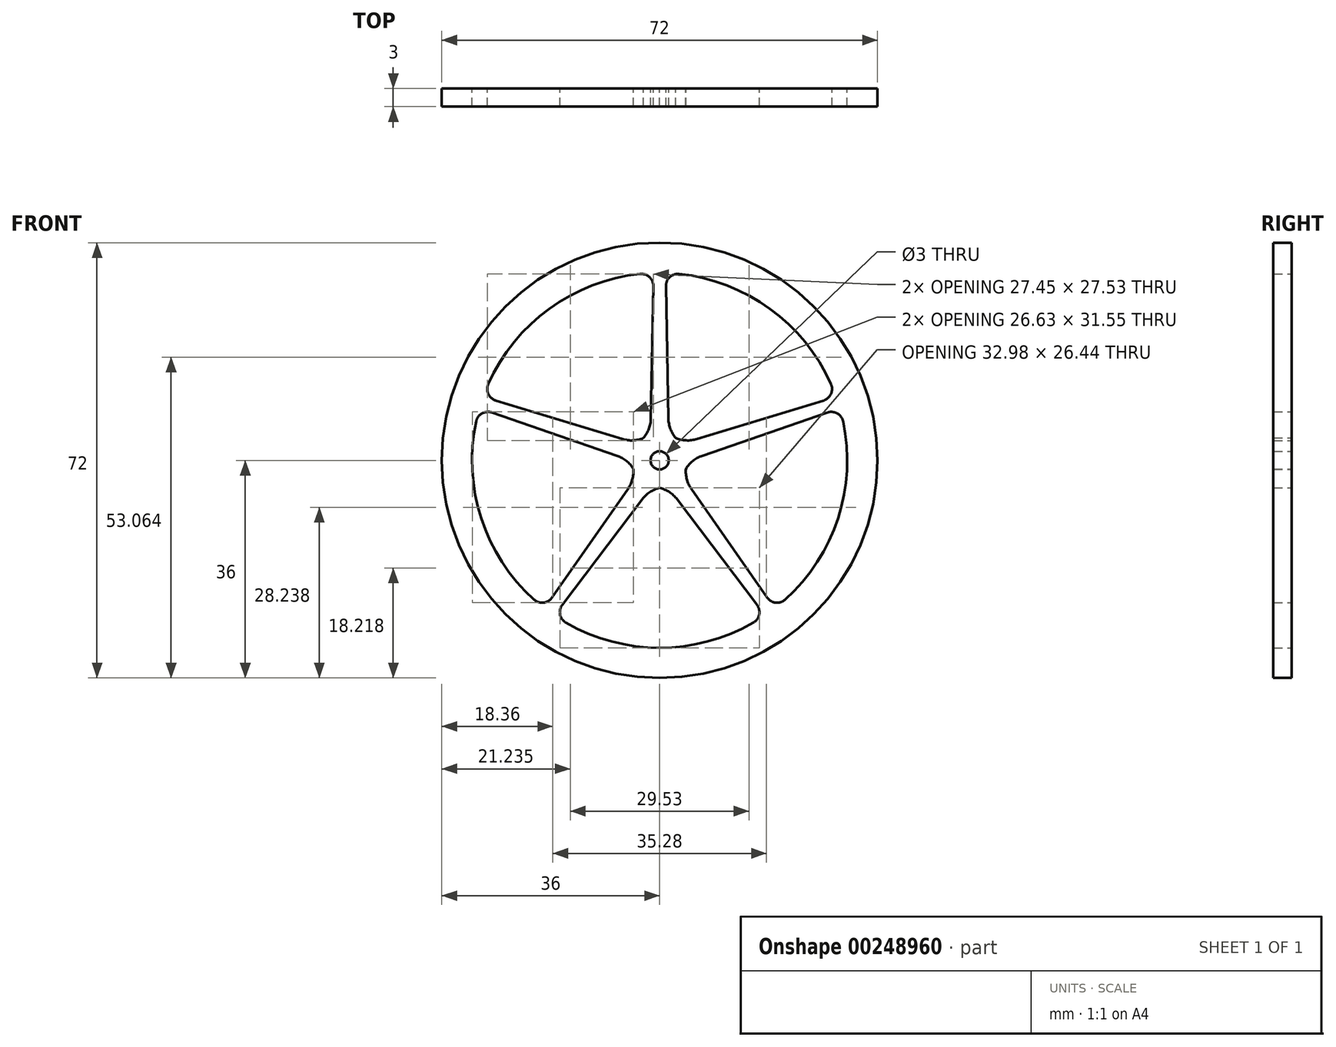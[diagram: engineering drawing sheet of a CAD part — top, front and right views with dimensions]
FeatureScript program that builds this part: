
annotation { "Feature Type Name" : "Feature", "Feature Type Description" : "" }
export const myFeature = defineFeature(function(context is Context, id is Id, definition is map)
    precondition{}
    {
        {
            var Q0;
            Q0=qCreatedBy(makeId("Front.planeOp"),FACE);
            var sketch = newSketch(context, id + "F0", { "sketchPlane" : qUnion([Q0])});
            skCircle(sketch, "E0", {"center": v(0, 0) * mm, "radius": 36 * mm});
            skCircle(sketch, "E1", {"center": v(0, 0) * mm, "radius": 1.5 * mm});
            skCircle(sketch, "E2", {"center": v(0, 0) * mm, "radius": 4.5 * mm});
            skCircle(sketch, "E3", {"center": v(0, 0) * mm, "radius": 31 * mm});
            skLineSegment(sketch, "E4", {"start": v(0, 0) * mm, "end": v(0, 1.5) * mm, "construction": true});
            skLineSegment(sketch, "E5", {"start": v(-1.5, 4.24) * mm, "end": v(-1, 30.98) * mm});
            skLineSegment(sketch, "E6.MirrorCS", {"start": v(1.5, 4.24) * mm, "end": v(1, 30.98) * mm});
            skPoint(sketch, "E7.trimOffspring.end.orphan", {"position": v(0, 31) * mm});
            skPoint(sketch, "E7.trimOffspring.start.orphan", {"position": v(0, 4.5) * mm});
            skSolve(sketch);
        }
        {
            var Q0;
            Q0=makeQuery(id+"F0.imprint","IMPRINT",FACE,{"disambiguationData":[TD([[makeQuery(id+"F0.imprint","IMPRINT",EDGE,{"derivedFrom":sQuery(id+"F0.wireOp",EDGE,"E0")}),1.0]])]});
            var Q1;
            {var subQ0=sQuery(id+"F0.wireOp",EDGE,"E5");Q1=makeQuery(id+"F0.imprint","IMPRINT",FACE,{"disambiguationData":[TD([[makeQuery(id+"F0.imprint","IMPRINT",EDGE,{"derivedFrom":subQ0}),-1.0]])]});}
            var Q2;
            Q2=makeQuery(id+"F0.imprint","IMPRINT",FACE,{"disambiguationData":[TD([[makeQuery(id+"F0.imprint","IMPRINT",EDGE,{"derivedFrom":sQuery(id+"F0.wireOp",EDGE,"E1")}),-1.0]])]});
            var Q3;
            Q3=sQuery(id+"F0.wireOp",EDGE,"E1");
            var Q4;
            Q4=sQuery(id+"F0.wireOp",EDGE,"E0");
            extrude(context, id + "F1", {"entities" : qUnion([Q0, Q1, Q2]), "surfaceEntities" : qUnion([Q3, Q4]), "depth" : 3 * mm});
        }
        {
            var Q0;
            Q0=makeQuery(id+"F1.opExtrude","SWEPT_EDGE",EDGE,{"disambiguationData":[OSD([sQuery(id+"F0.wireOp",EDGE,"E3"),sQuery(id+"F0.wireOp",EDGE,"E6.MirrorCS")])]});
            var Q1;
            Q1=makeQuery(id+"F1.opExtrude","SWEPT_EDGE",EDGE,{"disambiguationData":[OSD([sQuery(id+"F0.wireOp",EDGE,"E3"),sQuery(id+"F0.wireOp",EDGE,"E5")])]});
            fillet(context, id + "F2", {"entities" : qUnion([Q0, Q1]), "radius" : 2 * mm, "tangentPropagation" : true, "allowEdgeOverflow" : false});
        }
        {
            var Q0;
            Q0=makeQuery(id+"F1.opExtrude","SWEPT_EDGE",EDGE,{"disambiguationData":[OSD([sQuery(id+"F0.wireOp",EDGE,"E2"),sQuery(id+"F0.wireOp",EDGE,"E5")])]});
            var Q1;
            Q1=makeQuery(id+"F1.opExtrude","SWEPT_EDGE",EDGE,{"disambiguationData":[OSD([sQuery(id+"F0.wireOp",EDGE,"E2"),sQuery(id+"F0.wireOp",EDGE,"E6.MirrorCS")])]});
            fillet(context, id + "F3", {"entities" : qUnion([Q0, Q1]), "radius" : 5.08 * mm, "tangentPropagation" : true, "allowEdgeOverflow" : false});
        }
        {
            var Q0;
            Q0=makeQuery(id+"F1.opExtrude","SWEPT_BODY",BODY,{"disambiguationData":[OSD([sQuery(id+"F0.wireOp",EDGE,"E0"),sQuery(id+"F0.wireOp",EDGE,"E1"),sQuery(id+"F0.wireOp",EDGE,"E2"),sQuery(id+"F0.wireOp",EDGE,"E3"),sQuery(id+"F0.wireOp",EDGE,"E5"),sQuery(id+"F0.wireOp",EDGE,"E6.MirrorCS")])]});
            var Q1;
            Q1=makeQuery(id+"F1.opExtrude","SWEPT_FACE",FACE,{"disambiguationData":[OSD([sQuery(id+"F0.wireOp",EDGE,"E0")])]});
            circularPattern(context, id + "F4", {"operationType" : NewBodyOperationType.ADD, "entities" : qUnion([Q0]), "axis" : qUnion([Q1]), "angle" : 360 * degree, "instanceCount" : 5, "equalSpace" : true});
        }
    });
